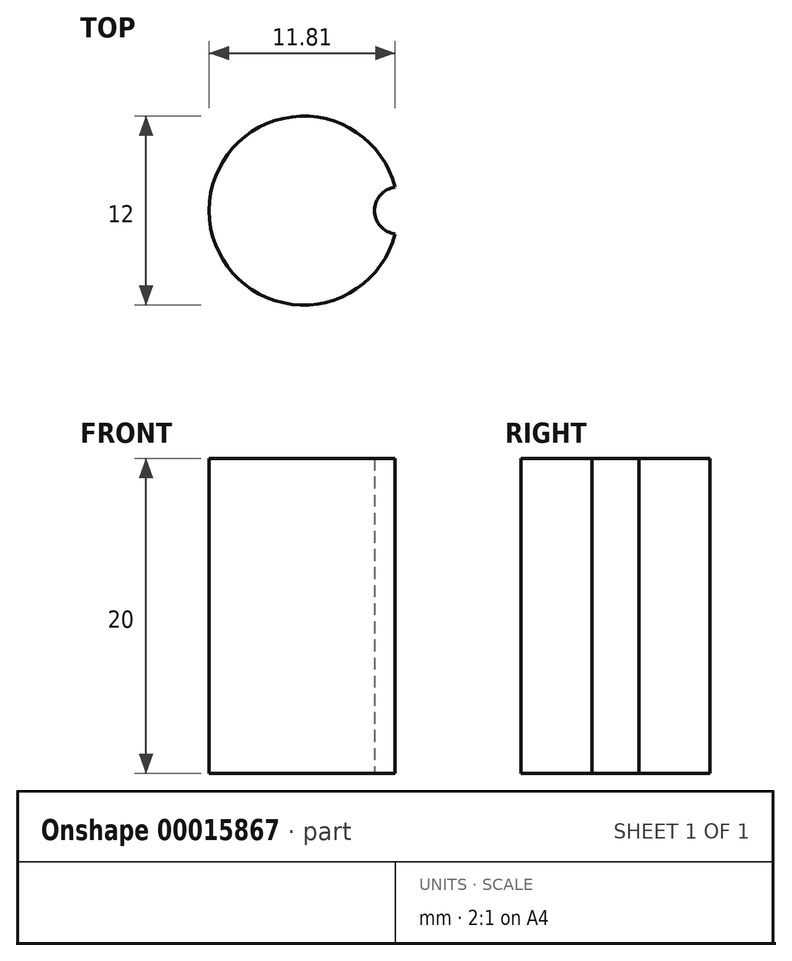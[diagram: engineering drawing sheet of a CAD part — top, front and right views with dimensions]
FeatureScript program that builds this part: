
annotation { "Feature Type Name" : "Feature", "Feature Type Description" : "" }
export const myFeature = defineFeature(function(context is Context, id is Id, definition is map)
    precondition{}
    {
        {
            var Q0;
            Q0=qCreatedBy(makeId("Top.planeOp"),FACE);
            var sketch = newSketch(context, id + "F0", { "sketchPlane" : qUnion([Q0])});
            skArc(sketch, "E0", {"start": v(5.81, 1.49) * mm, "mid": v(-6, 0) * mm, "end": v(5.81, -1.49) * mm});
            skArc(sketch, "E1", {"start": v(5.81, 1.49) * mm, "mid": v(4.5, 0) * mm, "end": v(5.81, -1.49) * mm});
            skSolve(sketch);
        }
        {
            var Q0;
            Q0 = qSketchRegion(id + "F0", true);
            extrude(context, id + "F1", {"entities" : qUnion([Q0]), "depth" : 20 * mm});
        }
    });
